# Revit family: LFX_A3-M-Pendant-Hemisphere
name_source: partatom
category: Lighting Fixtures
revit_build: Autodesk Revit 2016 (Build: 20150220_1215(x64)
units: mm (PartAtom-declared; Revit-internal decimal feet)

## family parameters
Always vertical = Yes
Cut with Voids When Loaded = No
Host = Ceiling
Light Source = Yes
Part Type = Normal
Room Calculation Point = No
Round Connector Dimension = Use Diameter
Shared = No

## types (4) — shared parameters
Ceiling Mount = Metal - Chrome
Color Filter = 16777215
Dimming Lamp Color Temperature Shift = <None>
Drop From Ceiling = 600 mm
Light Source Symbol Size = 609.6 mm  [stored 2 ft]
Pendant = Glass - Frosted

## per-type parameters (varying)
| type | Wattage Comments |
| 100 watt Incandescant | 100 |
| 150 watt Incandescant | 150 |
| Hemisphere | 100 |
| Hemisphere Pendant | 100 |

note: [stored X ft] marks values corroborated as IEEE doubles in the binary element streams (Revit-internal decimal feet)

## geometry (parser evidence)
native form markers: Sweep x1
no freeform markers — native parametric forms only
